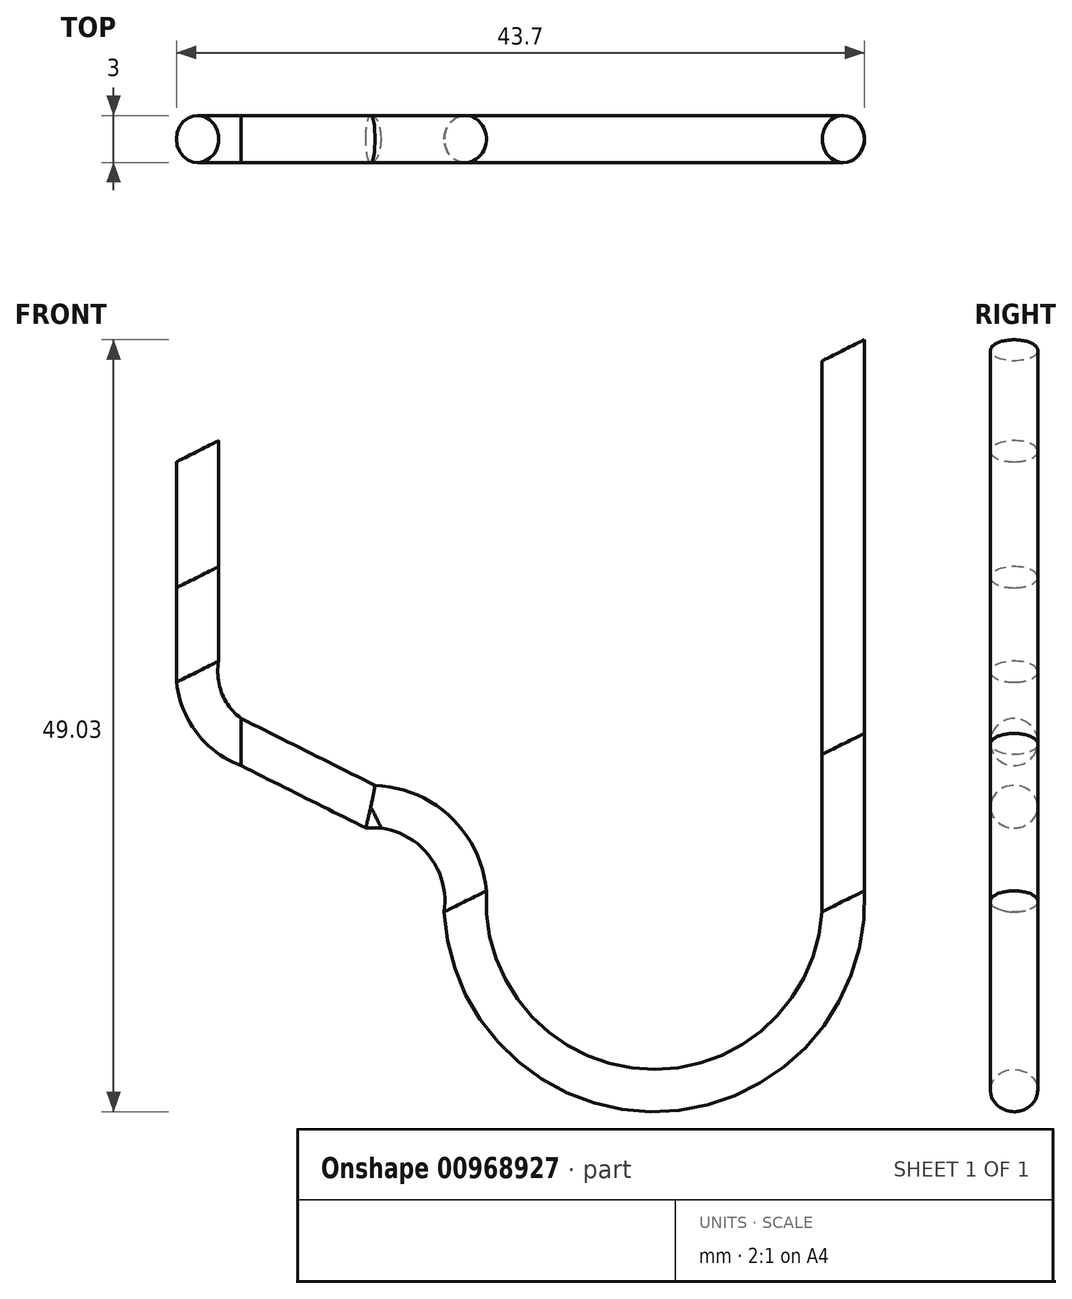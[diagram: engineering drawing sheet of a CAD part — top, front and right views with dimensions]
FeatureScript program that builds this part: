
annotation { "Feature Type Name" : "Feature", "Feature Type Description" : "" }
export const myFeature = defineFeature(function(context is Context, id is Id, definition is map)
    precondition{}
    {
        {
            var Q0;
            Q0=qCreatedBy(makeId("Front.planeOp"),FACE);
            var sketch = newSketch(context, id + "F0", { "sketchPlane" : qUnion([Q0])});
            skLineSegment(sketch, "E0", {"start": v(3, -0.82) * mm, "end": v(-5.24, 3.3) * mm});
            skLineSegment(sketch, "E1", {"start": v(-8, 7.77) * mm, "end": v(-8, 13.77) * mm});
            skPoint(sketch, "E2.visualSharp", {"position": v(-8, 4.68) * mm});
            skArc(sketch, "E2.filletArc", {"start": v(-8, 7.77) * mm, "mid": v(-7.25, 5.14) * mm, "end": v(-5.24, 3.3) * mm});
            skLineSegment(sketch, "E3", {"start": v(-8, 13.77) * mm, "end": v(-8, 21.77) * mm});
            skArc(sketch, "E4", {"start": v(9, -6.82) * mm, "mid": v(7.24, -2.58) * mm, "end": v(3, -0.82) * mm});
            skArc(sketch, "E5", {"start": v(9, -6.82) * mm, "mid": v(21, -18.82) * mm, "end": v(33, -6.82) * mm});
            skLineSegment(sketch, "E6", {"start": v(33, -6.82) * mm, "end": v(33, 3.18) * mm});
            skLineSegment(sketch, "E7", {"start": v(33, 3.18) * mm, "end": v(33, 28.18) * mm});
            skSolve(sketch);
        }
        {
            var Q0;
            Q0=qCreatedBy(makeId("Right.planeOp"),FACE);
            cPlane(context, id + "F1", {"entities" : qUnion([Q0]), "cplaneType" : CPlaneType.OFFSET, "offset" : 3 * mm, "width" : 150 * mm, "height" : 150 * mm});
        }
        {
            var Q0;
            Q0=qCreatedBy(id+"F1.planeOp",FACE);
            var sketch = newSketch(context, id + "F2", { "sketchPlane" : qUnion([Q0])});
            skCircle(sketch, "E8", {"center": v(0, -0.82) * mm, "radius": 1.5 * mm});
            skSolve(sketch);
        }
        {
            var Q0;
            Q0=makeQuery(id+"F2.imprint","IMPRINT",FACE,{"disambiguationData":[TD([[makeQuery(id+"F2.imprint","IMPRINT",EDGE,{"derivedFrom":sQuery(id+"F2.wireOp",EDGE,"E8")}),1.0]])]});
            var Q1;
            Q1=sQuery(id+"F0.wireOp",EDGE,"E0");
            var Q2;
            Q2=sQuery(id+"F0.wireOp",EDGE,"E2.filletArc");
            var Q3;
            Q3=sQuery(id+"F0.wireOp",EDGE,"E1");
            var Q4;
            Q4=sQuery(id+"F0.wireOp",EDGE,"E3");
            var Q5;
            Q5=sQuery(id+"F0.wireOp",EDGE,"E4");
            var Q6;
            Q6=sQuery(id+"F0.wireOp",EDGE,"E5");
            var Q7;
            Q7=sQuery(id+"F0.wireOp",EDGE,"E6");
            var Q8;
            Q8=sQuery(id+"F0.wireOp",EDGE,"E7");
            sweep(context, id + "F3", {"profiles" : qUnion([Q0]), "path" : qUnion([Q1, Q2, Q3, Q4, Q5, Q6, Q7, Q8])});
        }
    });
